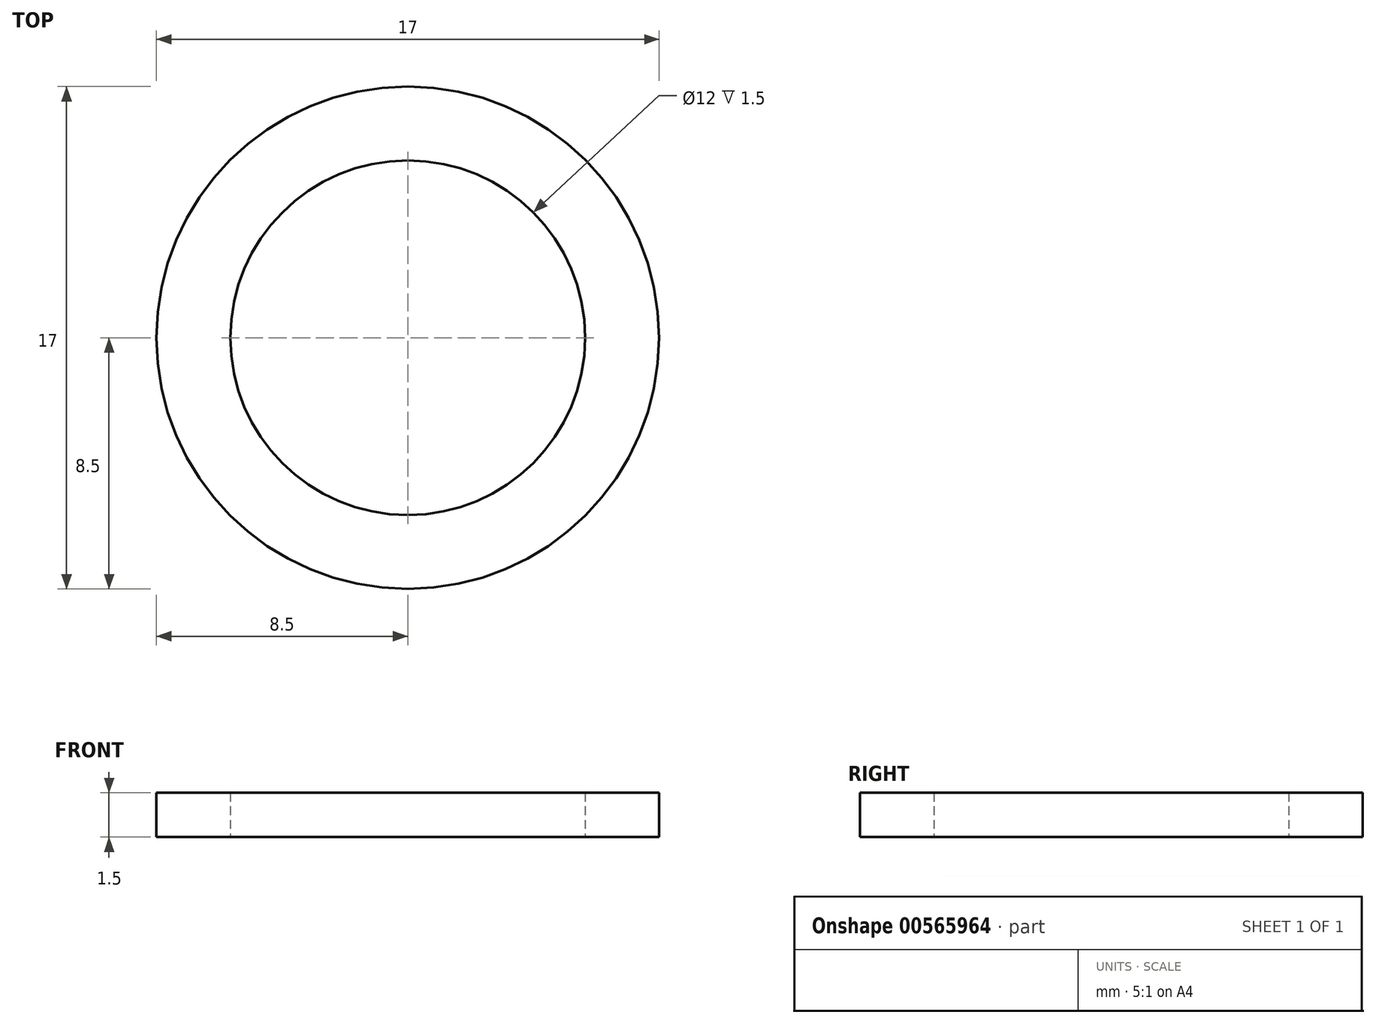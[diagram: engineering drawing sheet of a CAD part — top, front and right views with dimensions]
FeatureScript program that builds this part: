
annotation { "Feature Type Name" : "Feature", "Feature Type Description" : "" }
export const myFeature = defineFeature(function(context is Context, id is Id, definition is map)
    precondition{}
    {
        {
            var Q0;
            Q0=qCreatedBy(makeId("Top.planeOp"),FACE);
            var sketch = newSketch(context, id + "F0", { "sketchPlane" : qUnion([Q0])});
            skCircle(sketch, "E0", {"center": v(0, 0) * mm, "radius": 6 * mm});
            skCircle(sketch, "E1", {"center": v(0, 0) * mm, "radius": 8.5 * mm});
            skSolve(sketch);
        }
        {
            var Q0;
            Q0 = qSketchRegion(id + "F0", true);
            extrude(context, id + "F1", {"entities" : qUnion([Q0]), "depth" : 1.5 * mm, "offsetDistance" : 25 * mm});
        }
    });
